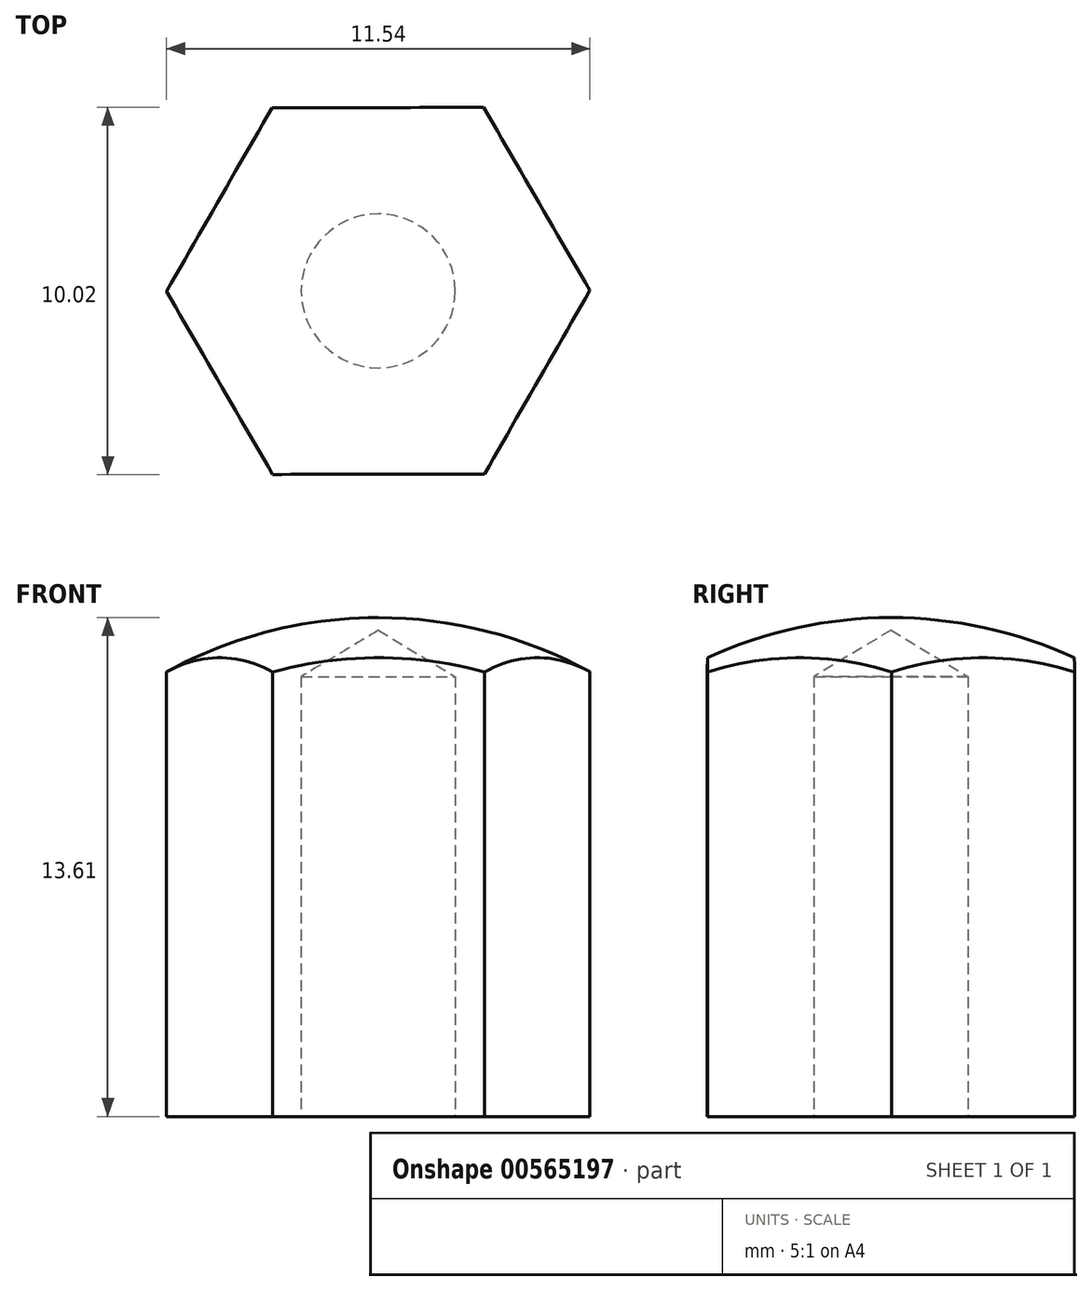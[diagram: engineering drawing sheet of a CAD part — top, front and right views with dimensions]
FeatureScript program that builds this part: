
annotation { "Feature Type Name" : "Feature", "Feature Type Description" : "" }
export const myFeature = defineFeature(function(context is Context, id is Id, definition is map)
    precondition{}
    {
        {
            var Q0;
            Q0=qCreatedBy(makeId("Front.planeOp"),FACE);
            var sketch = newSketch(context, id + "F0", { "sketchPlane" : qUnion([Q0])});
            skLineSegment(sketch, "E0", {"start": v(-6, 0) * mm, "end": v(-6, 12) * mm});
            skArc(sketch, "E1", {"start": v(0, 13.6) * mm, "mid": v(-3.1, 13.2) * mm, "end": v(-6, 12) * mm});
            skLineSegment(sketch, "E2", {"start": v(0, 13.6) * mm, "end": v(0, 0) * mm});
            skLineSegment(sketch, "E3", {"start": v(0, 0) * mm, "end": v(-6, 0) * mm});
            skSolve(sketch);
        }
        {
            var Q0;
            Q0=makeQuery(id+"F0.imprint","IMPRINT",FACE,{"disambiguationData":[TD([[makeQuery(id+"F0.imprint","IMPRINT",EDGE,{"derivedFrom":sQuery(id+"F0.wireOp",EDGE,"E0")}),-1.0]])]});
            var Q1;
            Q1=sQuery(id+"F0.wireOp",EDGE,"E2");
            revolve(context, id + "F1", {"entities" : qUnion([Q0]), "axis" : qUnion([Q1]), "revolveType" : RevolveType.FULL});
        }
        {
            var Q0;
            Q0=makeQuery(id+"F1.opRevolve","SWEPT_FACE",FACE,{"disambiguationData":[OSD([sQuery(id+"F0.wireOp",EDGE,"E3")])]});
            var sketch = newSketch(context, id + "F2", { "sketchPlane" : qUnion([Q0])});
            skPoint(sketch, "E4", {"position": v(0, 0) * mm});
            skSolve(sketch);
        }
        {
            var Q0;
            Q0=sQuery(id+"F2.wireOp",VERTEX,"E4");
            var Q1;
            Q1=makeQuery(id+"F1.opRevolve","SWEPT_BODY",BODY,{"disambiguationData":[OSD([sQuery(id+"F0.wireOp",EDGE,"E0"),sQuery(id+"F0.wireOp",EDGE,"E1"),sQuery(id+"F0.wireOp",EDGE,"E2"),sQuery(id+"F0.wireOp",EDGE,"E3")])]});
            hole(context, id + "F3", {"style" : HoleStyle.SIMPLE, "endStyle" : HoleEndStyle.BLIND, "standardTappedOrClearance" : lookupTablePath({ "standard" : "ISO", "engagement" : "75%", "pitch" : "0.8 mm", "size" : "M5", "type" : "Tapped" }), "standardBlindInLast" : lookupTablePath({ "standard" : "ISO", "engagement" : "75%", "pitch" : "0.8 mm", "size" : "M5", "type" : "Tapped" }), "holeDiameter" : 4.2 * mm, "showTappedDepth" : true, "holeDepth" : 12 * mm, "isTappedThrough" : true, "tappedDepth" : 12 * mm, "tapClearance" : 0, "startFromSketch" : true, "locations" : qUnion([Q0]), "scope" : qUnion([Q1]), "majorDiameter" : 5 * mm});
        }
        {
            var Q0;
            Q0=qCreatedBy(makeId("Top.planeOp"),FACE);
            var sketch = newSketch(context, id + "F4", { "sketchPlane" : qUnion([Q0])});
            skCircle(sketch, "E5.cCircle", {"center": v(0, 0) * mm, "radius": 5 * mm, "construction": true});
            skLineSegment(sketch, "E5.0", {"start": v(-5.77, -0.01) * mm, "end": v(-2.9, 5) * mm});
            skLineSegment(sketch, "E5.1", {"start": v(-2.9, 5) * mm, "end": v(2.88, 5) * mm});
            skLineSegment(sketch, "E5.2", {"start": v(2.88, 5) * mm, "end": v(5.77, 0.01) * mm});
            skLineSegment(sketch, "E5.3", {"start": v(5.77, 0.01) * mm, "end": v(2.9, -5) * mm});
            skLineSegment(sketch, "E5.4", {"start": v(2.9, -5) * mm, "end": v(-2.88, -5) * mm});
            skLineSegment(sketch, "E5.5", {"start": v(-2.88, -5) * mm, "end": v(-5.77, -0.01) * mm});
            skPoint(sketch, "E5.0.midPoint", {"position": v(-4.34, 2.5) * mm});
            skSolve(sketch);
        }
        {
            var Q0;
            Q0=makeQuery(id+"F4.imprint","IMPRINT",FACE,{"disambiguationData":[TD([[makeQuery(id+"F4.imprint","IMPRINT",EDGE,{"derivedFrom":sQuery(id+"F4.wireOp",EDGE,"E5.0")}),-1.0]])]});
            extrude(context, id + "F5", {"entities" : qUnion([Q0]), "operationType" : NewBodyOperationType.INTERSECT, "endBound" : BoundingType.THROUGH_ALL, "depth" : 25 * mm, "offsetDistance" : 25 * mm});
        }
    });
